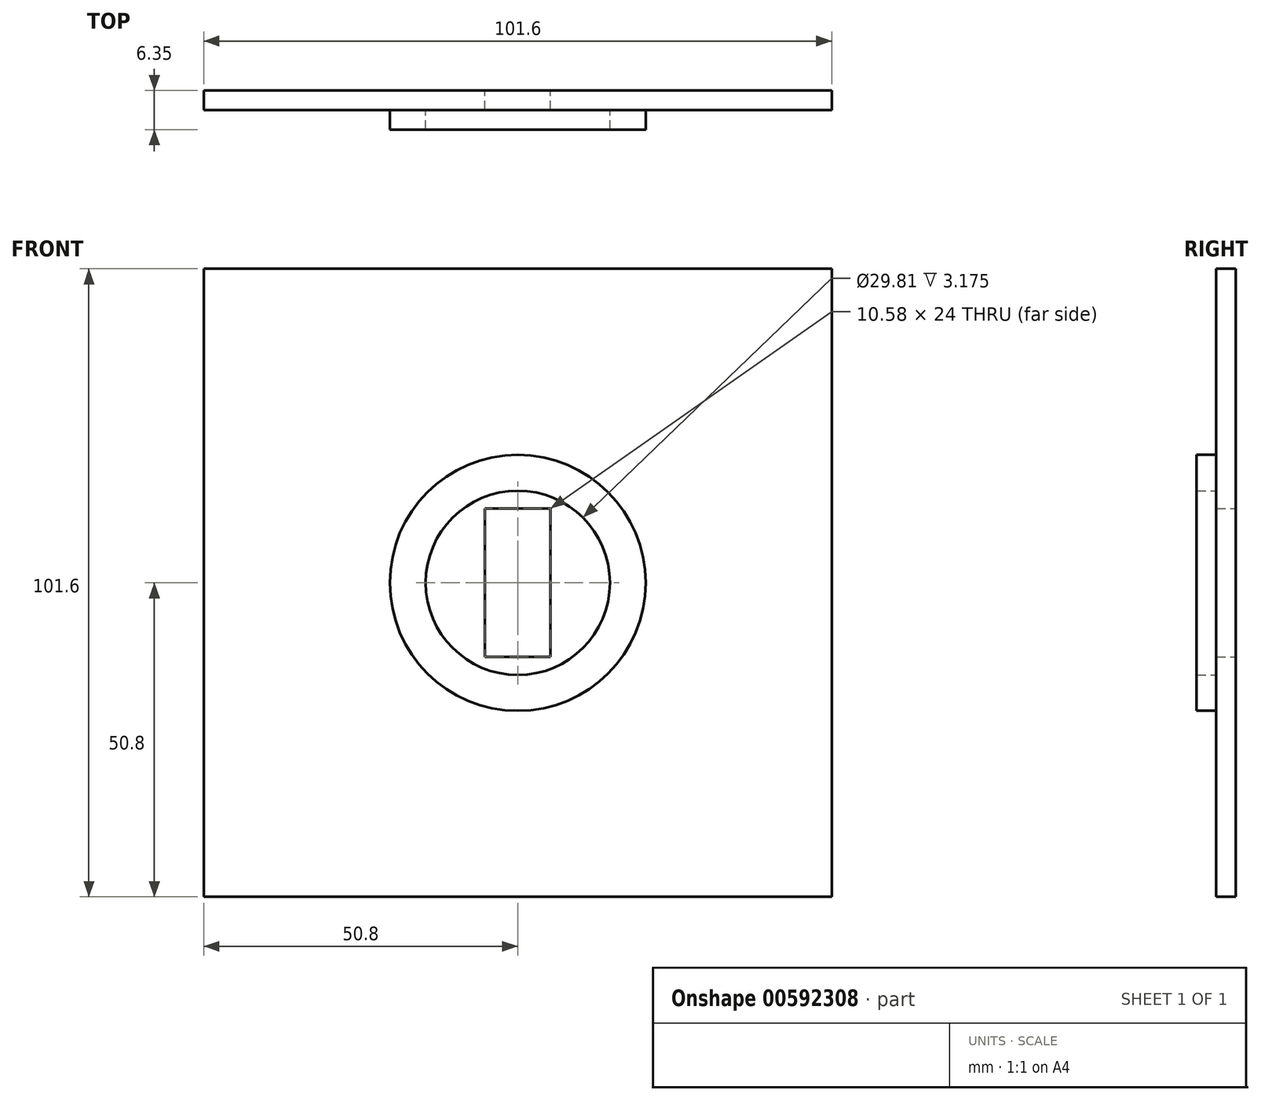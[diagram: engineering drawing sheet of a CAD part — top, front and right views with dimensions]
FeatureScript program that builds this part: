
annotation { "Feature Type Name" : "Feature", "Feature Type Description" : "" }
export const myFeature = defineFeature(function(context is Context, id is Id, definition is map)
    precondition{}
    {
        {
            var Q0;
            Q0=qCreatedBy(makeId("Front.planeOp"),FACE);
            var sketch = newSketch(context, id + "F0", { "sketchPlane" : qUnion([Q0])});
            skLineSegment(sketch, "E0.bottom", {"start": v(50.8, -50.8) * mm, "end": v(-50.8, -50.8) * mm});
            skLineSegment(sketch, "E0.top", {"start": v(50.8, 50.8) * mm, "end": v(-50.8, 50.8) * mm});
            skLineSegment(sketch, "E0.left", {"start": v(50.8, -50.8) * mm, "end": v(50.8, 50.8) * mm});
            skLineSegment(sketch, "E0.right", {"start": v(-50.8, -50.8) * mm, "end": v(-50.8, 50.8) * mm});
            skPoint(sketch, "E0.middle", {"position": v(0, 0) * mm});
            skLineSegment(sketch, "E1.bottom", {"start": v(5.3, -12) * mm, "end": v(-5.3, -12) * mm});
            skLineSegment(sketch, "E1.top", {"start": v(5.3, 12) * mm, "end": v(-5.3, 12) * mm});
            skLineSegment(sketch, "E1.left", {"start": v(5.3, -12) * mm, "end": v(5.3, 12) * mm});
            skLineSegment(sketch, "E1.right", {"start": v(-5.3, -12) * mm, "end": v(-5.3, 12) * mm});
            skSolve(sketch);
        }
        {
            var Q0;
            Q0 = qSketchRegion(id + "F0", true);
            extrude(context, id + "F1", {"entities" : qUnion([Q0]), "depth" : 3.17 * mm, "offsetDistance" : 25.4 * mm});
        }
        {
            var Q0;
            Q0=makeQuery(id+"F1.opExtrude","CAP_FACE",FACE,{"disambiguationData":[OSD([sQuery(id+"F0.wireOp",EDGE,"E0.bottom"),sQuery(id+"F0.wireOp",EDGE,"E0.top"),sQuery(id+"F0.wireOp",EDGE,"E0.left"),sQuery(id+"F0.wireOp",EDGE,"E0.right"),sQuery(id+"F0.wireOp",EDGE,"E1.bottom"),sQuery(id+"F0.wireOp",EDGE,"E1.top"),sQuery(id+"F0.wireOp",EDGE,"E1.left"),sQuery(id+"F0.wireOp",EDGE,"E1.right")])],"isStart":false});
            var sketch = newSketch(context, id + "F2", { "sketchPlane" : qUnion([Q0])});
            skCircle(sketch, "E2", {"center": v(0, 0) * mm, "radius": 14.9 * mm});
            skCircle(sketch, "E3", {"center": v(0, 0) * mm, "radius": 20.7 * mm});
            skSolve(sketch);
        }
        {
            var Q0;
            Q0 = qSketchRegion(id + "F2", true);
            extrude(context, id + "F3", {"entities" : qUnion([Q0]), "operationType" : NewBodyOperationType.ADD, "depth" : 3.17 * mm, "offsetDistance" : 25.4 * mm});
        }
    });
